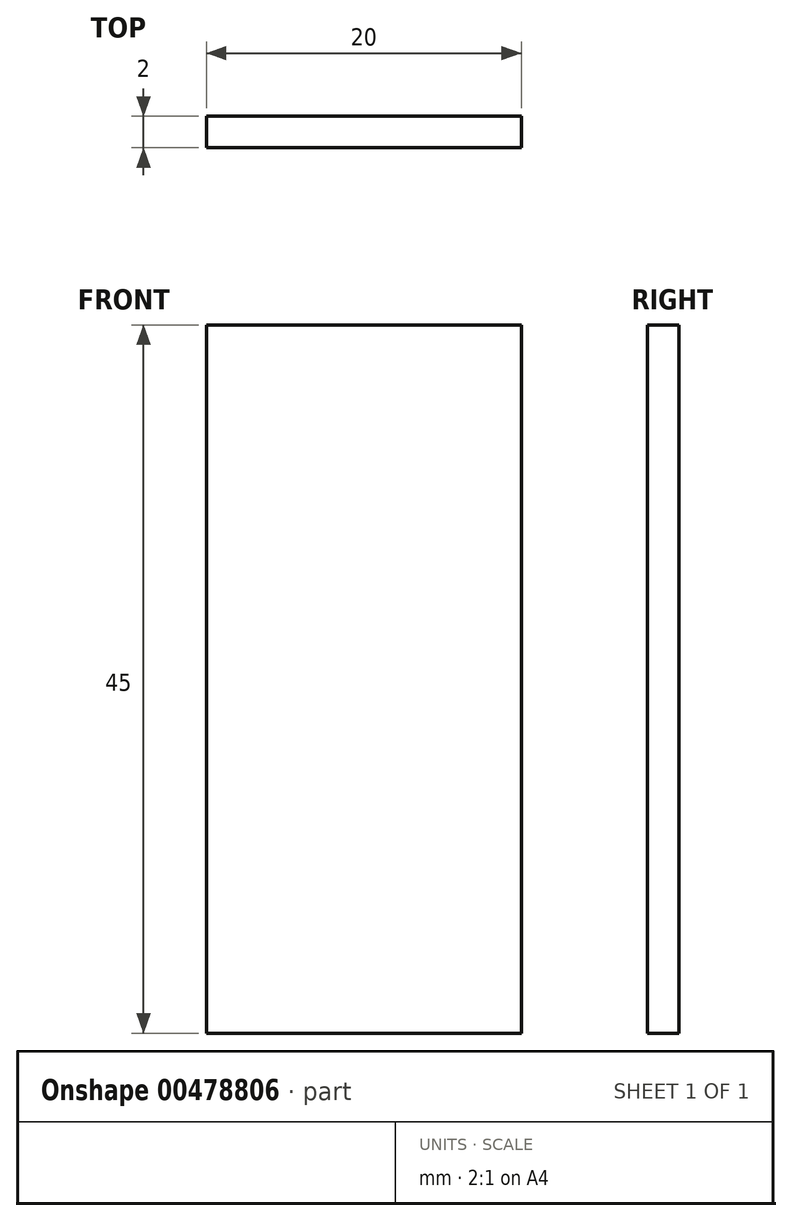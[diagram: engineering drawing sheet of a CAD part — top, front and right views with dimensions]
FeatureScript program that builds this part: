
annotation { "Feature Type Name" : "Feature", "Feature Type Description" : "" }
export const myFeature = defineFeature(function(context is Context, id is Id, definition is map)
    precondition{}
    {
        {
            var Q0;
            Q0=qCreatedBy(makeId("Front.planeOp"),FACE);
            var sketch = newSketch(context, id + "F0", { "sketchPlane" : qUnion([Q0])});
            skLineSegment(sketch, "E0.bottom", {"start": v(10, 22.5) * mm, "end": v(-10, 22.5) * mm});
            skLineSegment(sketch, "E0.top", {"start": v(10, -22.5) * mm, "end": v(-10, -22.5) * mm});
            skLineSegment(sketch, "E0.left", {"start": v(10, 22.5) * mm, "end": v(10, -22.5) * mm});
            skLineSegment(sketch, "E0.right", {"start": v(-10, 22.5) * mm, "end": v(-10, -22.5) * mm});
            skPoint(sketch, "E0.middle", {"position": v(0, 0) * mm});
            skSolve(sketch);
        }
        {
            var Q0;
            Q0 = qSketchRegion(id + "F0", true);
            extrude(context, id + "F1", {"entities" : qUnion([Q0]), "depth" : 2 * mm});
        }
    });
